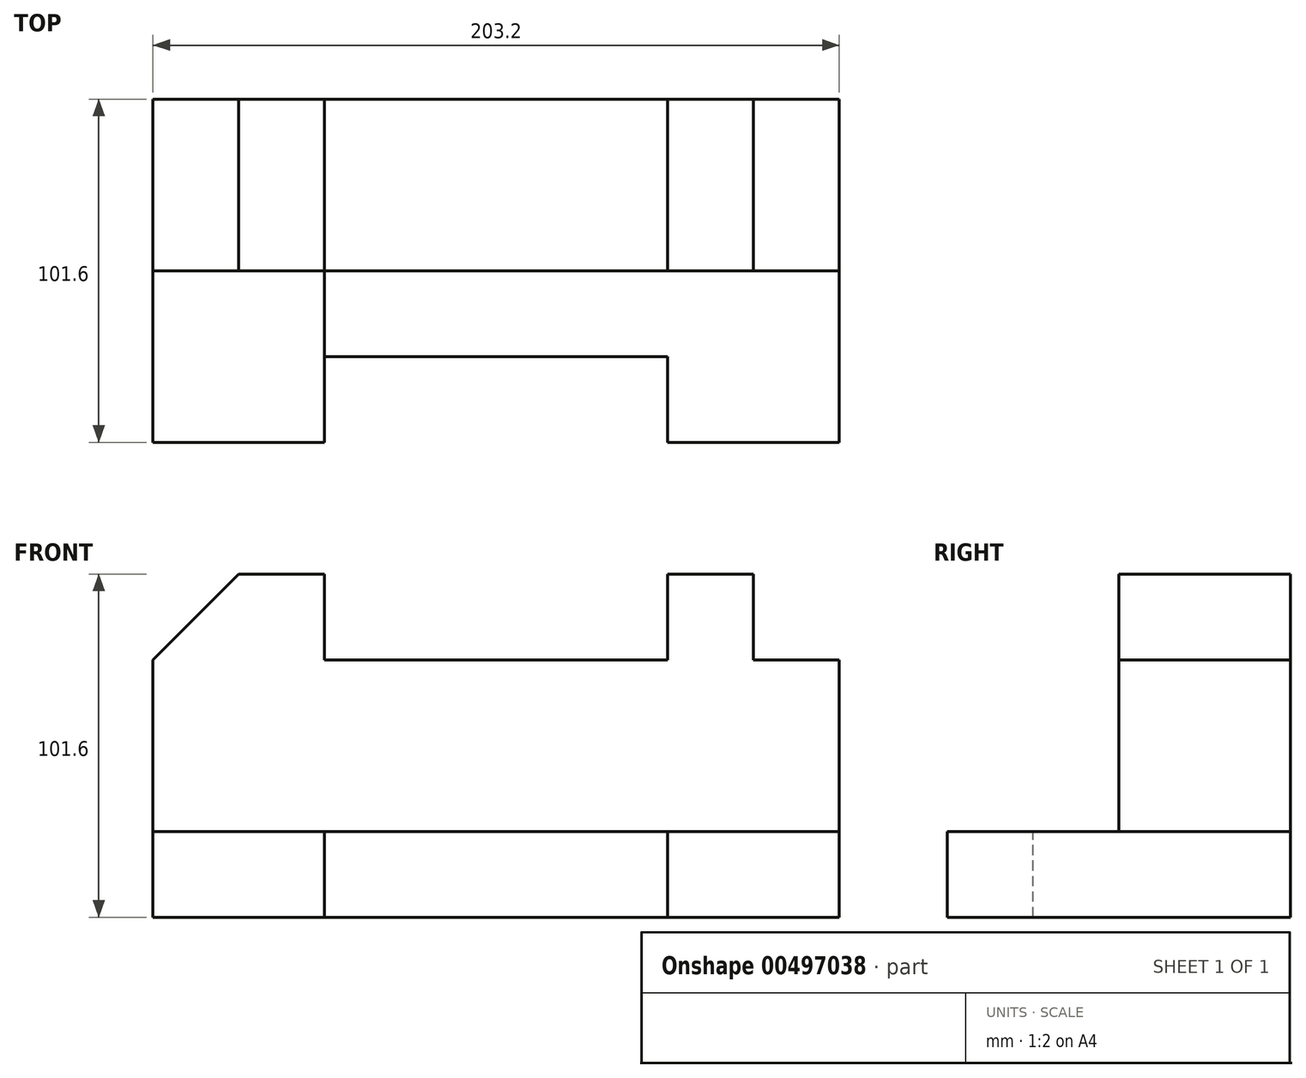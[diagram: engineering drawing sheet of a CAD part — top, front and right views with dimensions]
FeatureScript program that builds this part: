
annotation { "Feature Type Name" : "Feature", "Feature Type Description" : "" }
export const myFeature = defineFeature(function(context is Context, id is Id, definition is map)
    precondition{}
    {
        {
            var Q0;
            Q0=qCreatedBy(makeId("Front.planeOp"),FACE);
            var sketch = newSketch(context, id + "F0", { "sketchPlane" : qUnion([Q0])});
            skLineSegment(sketch, "E0.bottom", {"start": v(0, 0) * mm, "end": v(50.8, 0) * mm});
            skLineSegment(sketch, "E0.top", {"start": v(0, 25.4) * mm, "end": v(50.8, 25.4) * mm});
            skLineSegment(sketch, "E0.left", {"start": v(0, 0) * mm, "end": v(0, 25.4) * mm});
            skLineSegment(sketch, "E0.right", {"start": v(50.8, 0) * mm, "end": v(50.8, 25.4) * mm});
            skLineSegment(sketch, "E1.bottom", {"start": v(50.8, 0) * mm, "end": v(152.4, 0) * mm});
            skLineSegment(sketch, "E1.top", {"start": v(50.8, 25.4) * mm, "end": v(152.4, 25.4) * mm});
            skLineSegment(sketch, "E1.right", {"start": v(152.4, 0) * mm, "end": v(152.4, 25.4) * mm});
            skLineSegment(sketch, "E2.bottom", {"start": v(152.4, 0) * mm, "end": v(203.2, 0) * mm});
            skLineSegment(sketch, "E2.top", {"start": v(152.4, 25.4) * mm, "end": v(203.2, 25.4) * mm});
            skLineSegment(sketch, "E2.right", {"start": v(203.2, 0) * mm, "end": v(203.2, 25.4) * mm});
            skLineSegment(sketch, "E3.bottom", {"start": v(0, 25.4) * mm, "end": v(203.2, 25.4) * mm});
            skLineSegment(sketch, "E3.left", {"start": v(0, 25.4) * mm, "end": v(0, 76.2) * mm});
            skLineSegment(sketch, "E3.right", {"start": v(203.2, 25.4) * mm, "end": v(203.2, 76.2) * mm});
            skLineSegment(sketch, "E4.bottom", {"start": v(0, 76.2) * mm, "end": v(50.8, 76.2) * mm});
            skLineSegment(sketch, "E4.right", {"start": v(50.8, 76.2) * mm, "end": v(50.8, 101.6) * mm});
            skLineSegment(sketch, "E5", {"start": v(0, 76.2) * mm, "end": v(25.4, 101.6) * mm});
            skLineSegment(sketch, "E6", {"start": v(25.4, 101.6) * mm, "end": v(25.4, 76.2) * mm});
            skLineSegment(sketch, "E7", {"start": v(25.4, 101.6) * mm, "end": v(50.8, 101.6) * mm});
            skLineSegment(sketch, "E8", {"start": v(0, 76.2) * mm, "end": v(203.2, 76.2) * mm});
            skLineSegment(sketch, "E9", {"start": v(203.2, 76.2) * mm, "end": v(177.8, 76.2) * mm});
            skLineSegment(sketch, "E10", {"start": v(177.8, 76.2) * mm, "end": v(177.8, 101.6) * mm});
            skLineSegment(sketch, "E11", {"start": v(177.8, 101.6) * mm, "end": v(203.2, 76.2) * mm});
            skLineSegment(sketch, "E12", {"start": v(177.8, 101.6) * mm, "end": v(152.4, 101.6) * mm});
            skLineSegment(sketch, "E13", {"start": v(152.4, 101.6) * mm, "end": v(152.4, 76.2) * mm});
            skLineSegment(sketch, "E14", {"start": v(152.4, 76.2) * mm, "end": v(177.8, 76.2) * mm});
            skSolve(sketch);
        }
        {
            var Q0;
            Q0=makeQuery(id+"F0.imprint","IMPRINT",FACE,{"disambiguationData":[TD([[makeQuery(id+"F0.imprint","IMPRINT",EDGE,{"derivedFrom":sQuery(id+"F0.wireOp",EDGE,"E0.bottom")}),1.0]])]});
            extrude(context, id + "F1", {"entities" : qUnion([Q0]), "depth" : 101.6 * mm});
        }
        {
            var Q0;
            Q0=makeQuery(id+"F0.imprint","IMPRINT",FACE,{"disambiguationData":[TD([[makeQuery(id+"F0.imprint","IMPRINT",EDGE,{"derivedFrom":sQuery(id+"F0.wireOp",EDGE,"E1.bottom")}),1.0]])]});
            extrude(context, id + "F2", {"entities" : qUnion([Q0]), "depth" : 76.2 * mm});
        }
        {
            var Q0;
            Q0=makeQuery(id+"F0.imprint","IMPRINT",FACE,{"disambiguationData":[TD([[makeQuery(id+"F0.imprint","IMPRINT",EDGE,{"derivedFrom":sQuery(id+"F0.wireOp",EDGE,"E2.bottom")}),1.0]])]});
            extrude(context, id + "F3", {"entities" : qUnion([Q0]), "operationType" : NewBodyOperationType.ADD, "depth" : 101.6 * mm});
        }
        {
            var Q0;
            {var subQ0=sQuery(id+"F0.wireOp",EDGE,"E3.left");Q0=makeQuery(id+"F0.imprint","IMPRINT",FACE,{"disambiguationData":[TD([[makeQuery(id+"F0.imprint","IMPRINT",EDGE,{"derivedFrom":subQ0}),-1.0]])]});}
            var Q1;
            {var subQ0=sQuery(id+"F0.wireOp",EDGE,"E4.right");Q1=makeQuery(id+"F0.imprint","IMPRINT",FACE,{"disambiguationData":[TD([[makeQuery(id+"F0.imprint","IMPRINT",EDGE,{"derivedFrom":subQ0}),1.0]])]});}
            var Q2;
            {var subQ0=sQuery(id+"F0.wireOp",EDGE,"E5");Q2=makeQuery(id+"F0.imprint","IMPRINT",FACE,{"disambiguationData":[TD([[makeQuery(id+"F0.imprint","IMPRINT",EDGE,{"derivedFrom":subQ0}),-1.0]])]});}
            var Q3;
            Q3=makeQuery(id+"F0.imprint","IMPRINT",FACE,{"disambiguationData":[TD([[makeQuery(id+"F0.imprint","IMPRINT",EDGE,{"derivedFrom":sQuery(id+"F0.wireOp",EDGE,"E10")}),1.0]])]});
            var Q4;
            Q4=makeQuery(id+"F0.imprint","IMPRINT",FACE,{"disambiguationData":[TD([[makeQuery(id+"F0.imprint","IMPRINT",EDGE,{"derivedFrom":sQuery(id+"F0.wireOp",EDGE,"E9")}),-1.0]])]});
            extrude(context, id + "F4", {"entities" : qUnion([Q0, Q1, Q2, Q3, Q4]), "depth" : 50.8 * mm});
        }
    });
